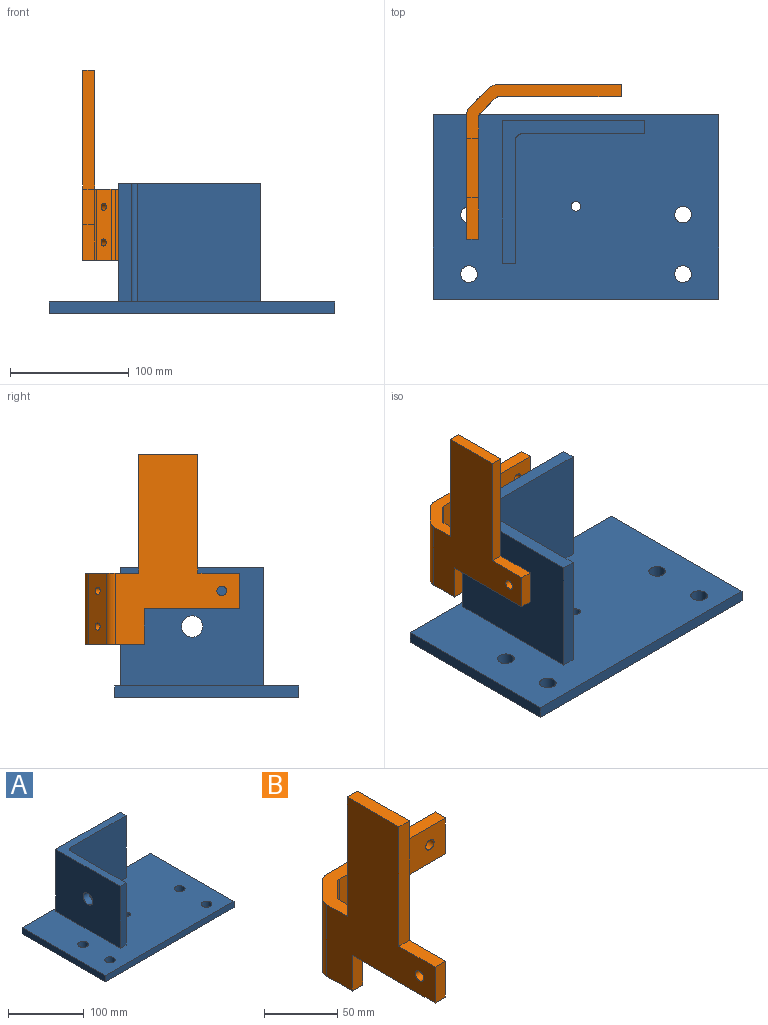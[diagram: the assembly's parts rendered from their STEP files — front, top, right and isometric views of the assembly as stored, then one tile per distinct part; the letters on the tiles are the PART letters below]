
ASSEMBLY  parts=2 mates=1
PART A: 20 faces, bbox 240x155x110 mm
  f0: plane 240x10mm, normal (0,1,0), area 2400mm2, adj f1,f7,f9,f10
  f1: plane 155x10mm, normal (-1,0,0), area 1550mm2, adj f0,f2,f9,f10
  f2: plane 240x10mm, normal (0,-1,0), area 2400mm2, adj f1,f7,f9,f10
  f3: cylinder r=7mm len=14mm, axis (0,0,1), area 439.8mm2, adj f9,f10
  f4: cylinder r=4mm len=10mm, axis (0,0,1), area 251.3mm2, adj f9,f10
  f5: cylinder r=7mm len=14mm, axis (0,0,1), area 439.8mm2, adj f9,f10
  f6: cylinder r=7mm len=14mm, axis (0,0,1), area 439.8mm2, adj f9,f10
  f7: plane 155x10mm, normal (1,0,0), area 1550mm2, adj f0,f2,f9,f10
  f8: cylinder r=7mm len=14mm, axis (0,0,1), area 439.8mm2, adj f9,f10
  f9: plane 240x155mm, normal (0,0,-1), area 36534mm2, adj f0,f1,f2,f3,f4,f5,f6,f7
  f10: plane 240x155mm, normal (0,0,1), area 34008.5mm2, adj f0,f1,f2,f3,f4,f5,f6,f7
  f11: plane 103.5x100mm, normal (0,-1,0), area 10350mm2, adj f10,f12,f17,f18
  f12: plane 100x11mm, normal (1,0,0), area 1100mm2, adj f10,f11,f13,f18
  f13: plane 120x100mm, normal (0,1,0), area 12000mm2, adj f10,f12,f14,f18
  f14: plane 120x100mm, normal (-1,0,0), area 11745.5mm2, adj f10,f13,f15,f18,f19
  f15: plane 100x11mm, normal (0,-1,0), area 1100mm2, adj f10,f14,f16,f18
  f16: plane 103.5x100mm, normal (1,0,0), area 10095.5mm2, adj f10,f15,f17,f18,f19
  f17: cylinder r=5.5mm len=100mm, axis (0,0,-1), area 863.9mm2, adj f10,f11,f16,f18
  f18: plane 120x120mm, normal (0,0,1), area 2525.5mm2, adj f11,f12,f13,f14,f15,f16,f17
  f19: cylinder r=9mm len=18mm, axis (1,0,0), area 622mm2, adj f14,f16
PART B: 26 faces, bbox 130x130x160 mm
  f0: plane 80x10mm, normal (0,0,-1), area 800mm2, adj f2,f3,f4,f22
  f1: plane 130x45mm, normal (0,0,1), area 1539.7mm2, adj f2,f4,f5,f6,f7,f8,f9,f10
  f2: plane 160x104.64mm, normal (-1,0,0), area 8828.4mm2, adj f0,f1,f3,f13,f15,f16,f17,f18
  f3: plane 30x10mm, normal (0,-1,0), area 300mm2, adj f0,f2,f4,f15
  f4: plane 160x102.57mm, normal (1,0,0), area 8704.2mm2, adj f0,f1,f3,f5,f15,f16,f17,f18
  f5: cylinder r=5mm len=60mm, axis (0,0,1), area 235.6mm2, adj f1,f4,f6,f23
  f6: plane 60x12.43mm, normal (0.71,-0.71,0), area 997.9mm2, adj f1,f5,f7,f23,f24,f25
  f7: cylinder r=5mm len=60mm, axis (0,0,1), area 235.6mm2, adj f1,f6,f8,f23
  f8: plane 102.57x60mm, normal (0,-1,0), area 3704.2mm2, adj f1,f7,f9,f14,f19,f21,f23
  f9: plane 30x10mm, normal (1,0,0), area 300mm2, adj f1,f8,f10,f14
  f10: plane 104.64x60mm, normal (0,1,0), area 3828.4mm2, adj f1,f9,f11,f14,f19,f21,f23
  f11: cylinder r=10mm len=60mm, axis (0,0,1), area 471.2mm2, adj f1,f10,f12,f23
  f12: plane 60x15.36mm, normal (-0.71,0.71,0), area 1246.4mm2, adj f1,f11,f13,f23,f24,f25
  f13: cylinder r=10mm len=60mm, axis (0,0,1), area 471.2mm2, adj f1,f2,f12,f23
  f14: plane 80x10mm, normal (0,0,-1), area 800mm2, adj f8,f9,f10,f21
  f15: plane 35x10mm, normal (0,0,1), area 350mm2, adj f2,f3,f4,f16
  f16: plane 100x10mm, normal (0,-1,0), area 1000mm2, adj f2,f4,f15,f18
  f17: plane 100x10mm, normal (0,1,0), area 1000mm2, adj f1,f2,f4,f18
  f18: plane 50x10mm, normal (0,0,1), area 500mm2, adj f2,f4,f16,f17
  f19: cylinder r=4mm len=10mm, axis (0,-1,0), area 251.3mm2, adj f8,f10
  f20: cylinder r=4mm len=10mm, axis (1,0,0), area 251.3mm2, adj f2,f4
  f21: plane 30x10mm, normal (1,0,0), area 300mm2, adj f8,f10,f14,f23
  f22: plane 30x10mm, normal (0,-1,0), area 300mm2, adj f0,f2,f4,f23
  f23: plane 50x50mm, normal (0,0,-1), area 789.7mm2, adj f2,f4,f5,f6,f7,f8,f10,f11
  f24: cylinder r=3mm len=11.31mm, axis (-0.71,0.71,0), area 188.5mm2, adj f6,f12
  f25: cylinder r=3mm len=11.31mm, axis (-0.71,0.71,0), area 188.5mm2, adj f6,f12
PLACE A t=(38.55,-30.59,145.27)mm
PLACE B t=(-54.88,25.17,240.27)mm
MATE parallel B.f15 <-> A.f18  axis (0,0,1) through (-42.59,-39.66,240.27)mm
